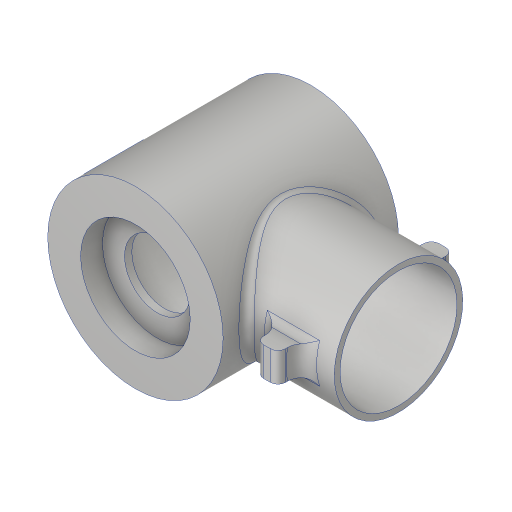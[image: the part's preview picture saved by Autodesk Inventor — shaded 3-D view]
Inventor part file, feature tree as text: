
AUTODESK INVENTOR PART (.ipt)
format: ipt  version: 2023.4 (Build 274418000, 418)  size: 349,184 bytes
history: native  units: in
note: dims shown in document units (in); Inventor stores cm internally (conversion verified against a paired STEP export)
features: sketch x8, extrude x6, plane x3, hole x2, fillet x2, mirror x1
ambient origin geometry x8: Origin, YZ Plane, XZ Plane, XY Plane, X Axis, Y Axis, Z Axis, Center Point
bodies: Solid1 (feature_tree)
feature tree (22):
  extrude  "Extrusion1"  Depth=3.0in TaperAngle=0.0deg
  plane  "Work Plane1"
  extrude  "Extrusion2"  Depth=2.0in
  extrude  "Extrusion3"  Depth=3.0in TaperAngle=0.0deg
  hole  "Hole1"  [1 undecoded]
  plane  "Work Plane2"
  extrude  "Extrusion4"  Depth=0.5in
  mirror  "Mirror1"
  plane  "Work Plane3"
  extrude  "Extrusion5"  [1 undecoded]
  fillet  "Fillet1"  Radius=0.5in
  fillet  "Fillet2"  Radius=1.25in
  hole  "Hole2"  [1 undecoded]
  extrude  "Extrusion6"  Depth=2.0in
  sketch  "Sketch1"  dims[d0=3.0in d1=3.0in d2=0.0in]
  sketch  "Sketch2"  dims[d3=3.0in d4=2.0in]
  sketch  "Sketch3"  dims[d5=0.1in d6=3.0in d7=0.0in]
  sketch  "Sketch4"  dims[d8=3.3in d9=0.0in]
  sketch  "Sketch6"  dims[d11=1.125in d12=0.75in d13=1.875in d14=0.375in d15=0.5635in d16=1.625in d17=0.8108in d22=1.5in]
  sketch  "Sketch7"  dims[d23=0.375in d24=0.5in]
  sketch  "Sketch8"  dims[d25=0.5in d26=0.0in d27=-1.875in d28=0.5in d29=1.25in]
  sketch  "Sketch9"  dims[d30=1.0in d31=0.0in d32=0.26in d33=0.13in d34=1.125in d35=0.75in d36=1.875in d37=0.375in d38=0.5635in d39=1.0in d40=0.8108in d41=2.0in d42=0.0in d43=0.5in d44=0.0344in d45=0.5in d46=0.0344in]
note: 3 required parameter values undecoded (feature->parameter linkage not recoverable at this tier; creation-order binding heuristic only, values carry confidence <= 0.55)
